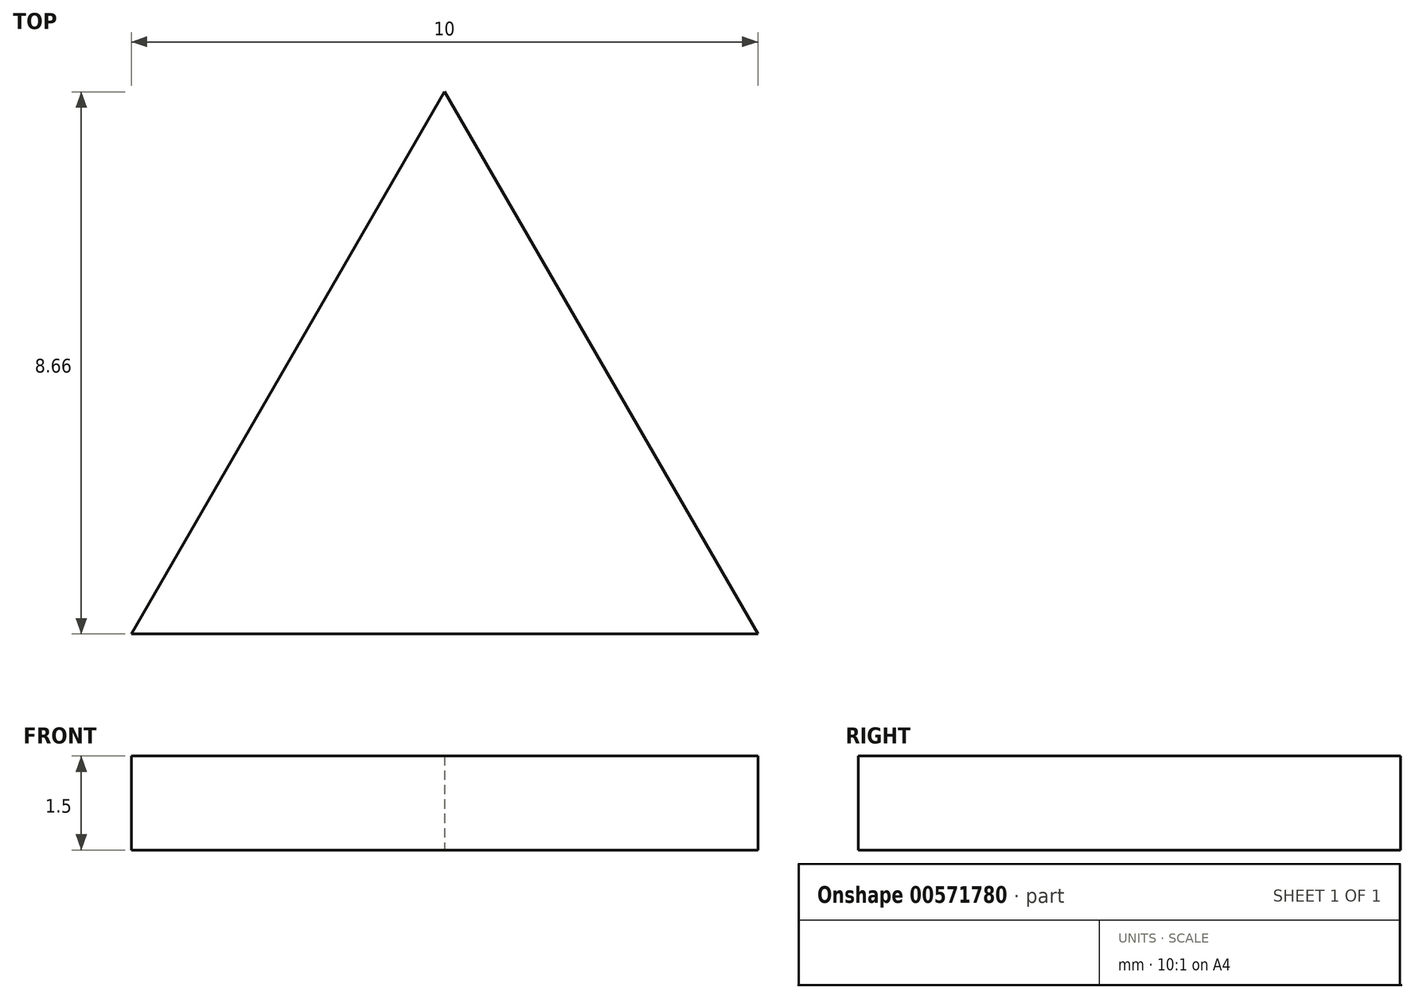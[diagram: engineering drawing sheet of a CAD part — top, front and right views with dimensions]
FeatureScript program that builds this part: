
annotation { "Feature Type Name" : "Feature", "Feature Type Description" : "" }
export const myFeature = defineFeature(function(context is Context, id is Id, definition is map)
    precondition{}
    {
        {
            var Q0;
            Q0=qCreatedBy(makeId("Top.planeOp"),FACE);
            var sketch = newSketch(context, id + "F0", { "sketchPlane" : qUnion([Q0])});
            skLineSegment(sketch, "E0", {"start": v(0, 0) * mm, "end": v(10, 0) * mm});
            skLineSegment(sketch, "E1", {"start": v(10, 0) * mm, "end": v(5, 8.66) * mm});
            skLineSegment(sketch, "E2", {"start": v(5, 8.66) * mm, "end": v(0, 0) * mm});
            skSolve(sketch);
        }
        {
            var Q0;
            Q0 = qSketchRegion(id + "F0", true);
            extrude(context, id + "F1", {"entities" : qUnion([Q0]), "depth" : 1.5 * mm, "offsetDistance" : 25 * mm});
        }
    });
